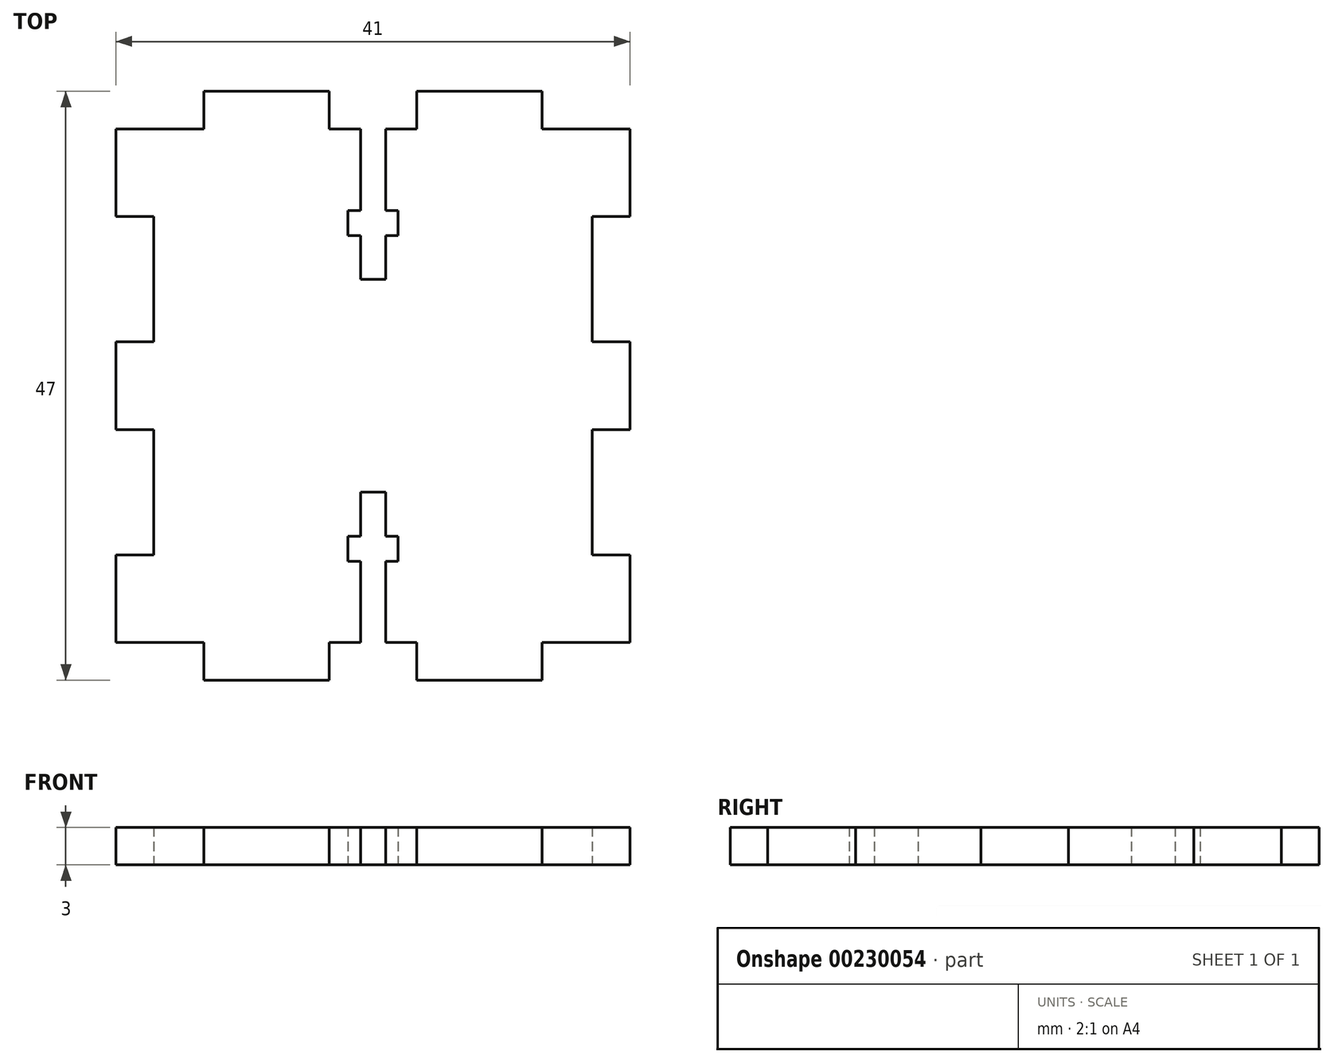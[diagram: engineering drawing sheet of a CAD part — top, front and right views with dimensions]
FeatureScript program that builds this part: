
annotation { "Feature Type Name" : "Feature", "Feature Type Description" : "" }
export const myFeature = defineFeature(function(context is Context, id is Id, definition is map)
    precondition{}
    {
        {
            var Q0;
            Q0=qCreatedBy(makeId("Top.planeOp"),FACE);
            var sketch = newSketch(context, id + "F0", { "sketchPlane" : qUnion([Q0])});
            skLineSegment(sketch, "E0", {"start": v(0, 0) * mm, "end": v(7, 0) * mm});
            skLineSegment(sketch, "E1", {"start": v(7, 0) * mm, "end": v(7, -3) * mm});
            skLineSegment(sketch, "E2", {"start": v(7, -3) * mm, "end": v(17, -3) * mm});
            skLineSegment(sketch, "E3", {"start": v(17, -3) * mm, "end": v(17, 0) * mm});
            skLineSegment(sketch, "E4", {"start": v(24, 0) * mm, "end": v(24, -3) * mm});
            skLineSegment(sketch, "E5", {"start": v(24, -3) * mm, "end": v(34, -3) * mm});
            skLineSegment(sketch, "E6", {"start": v(34, -3) * mm, "end": v(34, 0) * mm});
            skLineSegment(sketch, "E7", {"start": v(34, 0) * mm, "end": v(41, 0) * mm});
            skLineSegment(sketch, "E8", {"start": v(41, 0) * mm, "end": v(41, 7) * mm});
            skLineSegment(sketch, "E9", {"start": v(41, 7) * mm, "end": v(38, 7) * mm});
            skLineSegment(sketch, "E10", {"start": v(38, 7) * mm, "end": v(38, 17) * mm});
            skLineSegment(sketch, "E11", {"start": v(38, 17) * mm, "end": v(41, 17) * mm});
            skLineSegment(sketch, "E12", {"start": v(41, 17) * mm, "end": v(41, 24) * mm});
            skLineSegment(sketch, "E13", {"start": v(41, 24) * mm, "end": v(38, 24) * mm});
            skLineSegment(sketch, "E14", {"start": v(38, 24) * mm, "end": v(38, 34) * mm});
            skLineSegment(sketch, "E15", {"start": v(38, 34) * mm, "end": v(41, 34) * mm});
            skLineSegment(sketch, "E16", {"start": v(41, 34) * mm, "end": v(41, 41) * mm});
            skLineSegment(sketch, "E17", {"start": v(41, 41) * mm, "end": v(34, 41) * mm});
            skLineSegment(sketch, "E18", {"start": v(34, 41) * mm, "end": v(34, 44) * mm});
            skLineSegment(sketch, "E19", {"start": v(34, 44) * mm, "end": v(24, 44) * mm});
            skLineSegment(sketch, "E20", {"start": v(24, 44) * mm, "end": v(24, 41) * mm});
            skLineSegment(sketch, "E21", {"start": v(17, 41) * mm, "end": v(17, 44) * mm});
            skLineSegment(sketch, "E22", {"start": v(17, 44) * mm, "end": v(7, 44) * mm});
            skLineSegment(sketch, "E23", {"start": v(7, 44) * mm, "end": v(7, 41) * mm});
            skLineSegment(sketch, "E24", {"start": v(7, 41) * mm, "end": v(0, 41) * mm});
            skLineSegment(sketch, "E25", {"start": v(0, 41) * mm, "end": v(0, 34) * mm});
            skLineSegment(sketch, "E26", {"start": v(0, 34) * mm, "end": v(3, 34) * mm});
            skLineSegment(sketch, "E27", {"start": v(3, 34) * mm, "end": v(3, 24) * mm});
            skLineSegment(sketch, "E28", {"start": v(3, 24) * mm, "end": v(0, 24) * mm});
            skLineSegment(sketch, "E29", {"start": v(0, 24) * mm, "end": v(0, 17) * mm});
            skLineSegment(sketch, "E30", {"start": v(0, 17) * mm, "end": v(3, 17) * mm});
            skLineSegment(sketch, "E31", {"start": v(3, 17) * mm, "end": v(3, 7) * mm});
            skLineSegment(sketch, "E32", {"start": v(3, 7) * mm, "end": v(0, 7) * mm});
            skLineSegment(sketch, "E33", {"start": v(0, 7) * mm, "end": v(0, 0) * mm});
            skLineSegment(sketch, "E34.top", {"start": v(21.5, 29) * mm, "end": v(19.5, 29) * mm});
            skLineSegment(sketch, "E35.left", {"start": v(18.5, 34.5) * mm, "end": v(18.5, 32.5) * mm});
            skLineSegment(sketch, "E35.right", {"start": v(22.5, 34.5) * mm, "end": v(22.5, 32.5) * mm});
            skLineSegment(sketch, "E36", {"start": v(19.5, 41) * mm, "end": v(17, 41) * mm});
            skLineSegment(sketch, "E37", {"start": v(21.5, 41) * mm, "end": v(24, 41) * mm});
            skLineSegment(sketch, "E38", {"start": v(18.5, 34.5) * mm, "end": v(19.5, 34.5) * mm});
            skLineSegment(sketch, "E39", {"start": v(18.5, 32.5) * mm, "end": v(19.5, 32.5) * mm});
            skLineSegment(sketch, "E40", {"start": v(19.5, 41) * mm, "end": v(19.5, 34.5) * mm});
            skLineSegment(sketch, "E41", {"start": v(19.5, 32.5) * mm, "end": v(19.5, 29) * mm});
            skLineSegment(sketch, "E42", {"start": v(22.5, 34.5) * mm, "end": v(21.5, 34.5) * mm});
            skLineSegment(sketch, "E43", {"start": v(22.5, 32.5) * mm, "end": v(21.5, 32.5) * mm});
            skLineSegment(sketch, "E44", {"start": v(21.5, 41) * mm, "end": v(21.5, 34.5) * mm});
            skLineSegment(sketch, "E45", {"start": v(21.5, 32.5) * mm, "end": v(21.5, 29) * mm});
            skLineSegment(sketch, "E46.MirrorCS", {"start": v(22.5, 6.5) * mm, "end": v(21.5, 6.5) * mm});
            skLineSegment(sketch, "E47.MirrorCS", {"start": v(22.5, 8.5) * mm, "end": v(21.5, 8.5) * mm});
            skLineSegment(sketch, "E48.MirrorCS", {"start": v(19.5, 8.5) * mm, "end": v(19.5, 12) * mm});
            skLineSegment(sketch, "E49.MirrorCS", {"start": v(21.5, 12) * mm, "end": v(19.5, 12) * mm});
            skLineSegment(sketch, "E50.MirrorCS", {"start": v(19.5, 0) * mm, "end": v(19.5, 6.5) * mm});
            skLineSegment(sketch, "E51.MirrorCS", {"start": v(21.5, 0) * mm, "end": v(21.5, 6.5) * mm});
            skLineSegment(sketch, "E52.MirrorCS", {"start": v(22.5, 6.5) * mm, "end": v(22.5, 8.5) * mm});
            skLineSegment(sketch, "E53.MirrorCS", {"start": v(21.5, 8.5) * mm, "end": v(21.5, 12) * mm});
            skLineSegment(sketch, "E54.MirrorCS", {"start": v(18.5, 8.5) * mm, "end": v(19.5, 8.5) * mm});
            skLineSegment(sketch, "E55.MirrorCS", {"start": v(18.5, 6.5) * mm, "end": v(19.5, 6.5) * mm});
            skLineSegment(sketch, "E56.MirrorCS", {"start": v(18.5, 6.5) * mm, "end": v(18.5, 8.5) * mm});
            skLineSegment(sketch, "E57", {"start": v(17, 0) * mm, "end": v(19.5, 0) * mm});
            skLineSegment(sketch, "E58", {"start": v(21.5, 0) * mm, "end": v(24, 0) * mm});
            skSolve(sketch);
        }
        {
            var Q0;
            Q0 = qSketchRegion(id + "F0", true);
            extrude(context, id + "F1", {"entities" : qUnion([Q0]), "depth" : 3 * mm});
        }
    });
